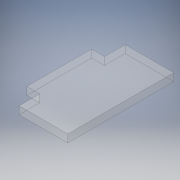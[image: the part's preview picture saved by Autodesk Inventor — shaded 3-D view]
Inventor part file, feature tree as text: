
AUTODESK INVENTOR PART (.ipt)
format: ipt  version: 2019 (Build 230136000, 136)  size: 122,368 bytes
history: native  units: in
note: dims shown in document units (in); Inventor stores cm internally (conversion verified against a paired STEP export)
features: extrude x1, sketch x1
ambient origin geometry x8: Origin, YZ Plane, XZ Plane, XY Plane, X Axis, Y Axis, Z Axis, Center Point
bodies: Solid1 (feature_tree)
feature tree (2):
  extrude  "Extrusion1"  Depth=0.1181in TaperAngle=0.0deg
  sketch  "Sketch1"  dims[d0=1.4961in d1=0.9843in d2=1.4961in d3=0.9843in d4=0.0787in d5=0.0787in d6=0.0591in d7=0.0591in d8=0.0591in d9=0.0591in d10=0.0591in d11=0.0591in d12=0.0591in d13=0.1181in d14=0.0in]
